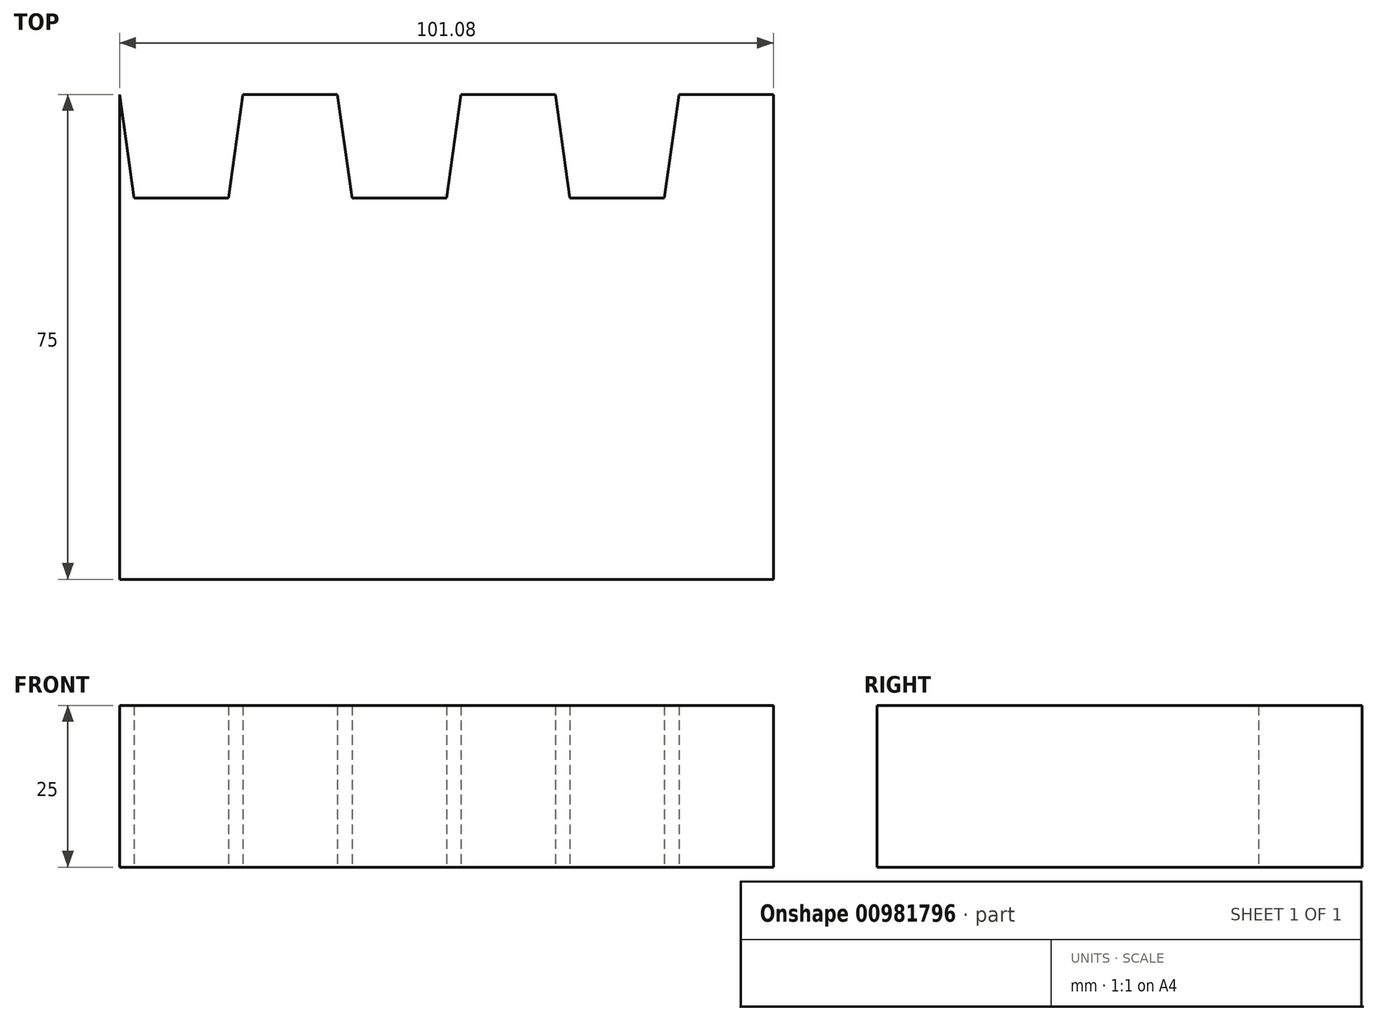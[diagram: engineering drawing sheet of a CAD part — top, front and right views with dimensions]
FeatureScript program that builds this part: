
annotation { "Feature Type Name" : "Feature", "Feature Type Description" : "" }
export const myFeature = defineFeature(function(context is Context, id is Id, definition is map)
    precondition{}
    {
        {
            var Q0;
            Q0=qCreatedBy(makeId("Top.planeOp"),FACE);
            var sketch = newSketch(context, id + "F0", { "sketchPlane" : qUnion([Q0])});
            skLineSegment(sketch, "E0", {"start": v(0, 0) * mm, "end": v(0, 75) * mm});
            skLineSegment(sketch, "E1", {"start": v(0, 0) * mm, "end": v(101.08, 0) * mm});
            skLineSegment(sketch, "E2", {"start": v(0, 75) * mm, "end": v(2.25, 59) * mm});
            skLineSegment(sketch, "E3", {"start": v(2.25, 59) * mm, "end": v(16.85, 59) * mm});
            skLineSegment(sketch, "E4", {"start": v(16.85, 59) * mm, "end": v(19.1, 75) * mm});
            skLineSegment(sketch, "E5", {"start": v(19.1, 75) * mm, "end": v(33.7, 75) * mm});
            skLineSegment(sketch, "E6.1.0.0", {"start": v(33.7, 75) * mm, "end": v(35.94, 59) * mm});
            skLineSegment(sketch, "E6.1.0.1", {"start": v(35.94, 59) * mm, "end": v(50.54, 59) * mm});
            skLineSegment(sketch, "E6.1.0.2", {"start": v(50.54, 59) * mm, "end": v(52.8, 75) * mm});
            skLineSegment(sketch, "E6.1.0.3", {"start": v(52.8, 75) * mm, "end": v(67.39, 75) * mm});
            skLineSegment(sketch, "E6.2.0.0", {"start": v(67.39, 75) * mm, "end": v(69.64, 59) * mm});
            skLineSegment(sketch, "E6.2.0.1", {"start": v(69.64, 59) * mm, "end": v(84.24, 59) * mm});
            skLineSegment(sketch, "E6.2.0.2", {"start": v(84.24, 59) * mm, "end": v(86.49, 75) * mm});
            skLineSegment(sketch, "E6.2.0.3", {"start": v(86.49, 75) * mm, "end": v(101.08, 75) * mm});
            skLineSegment(sketch, "E6.direction1", {"start": v(2.25, 59) * mm, "end": v(35.94, 59) * mm, "construction": true});
            skLineSegment(sketch, "E7", {"start": v(101.08, 75) * mm, "end": v(101.08, 0) * mm});
            skSolve(sketch);
        }
        {
            var Q0;
            Q0=makeQuery(id+"F0.imprint","IMPRINT",FACE,{"disambiguationData":[TD([[makeQuery(id+"F0.imprint","IMPRINT",EDGE,{"derivedFrom":sQuery(id+"F0.wireOp",EDGE,"E0")}),-1.0]])]});
            extrude(context, id + "F1", {"entities" : qUnion([Q0]), "depth" : 25 * mm, "offsetDistance" : 25 * mm});
        }
    });
